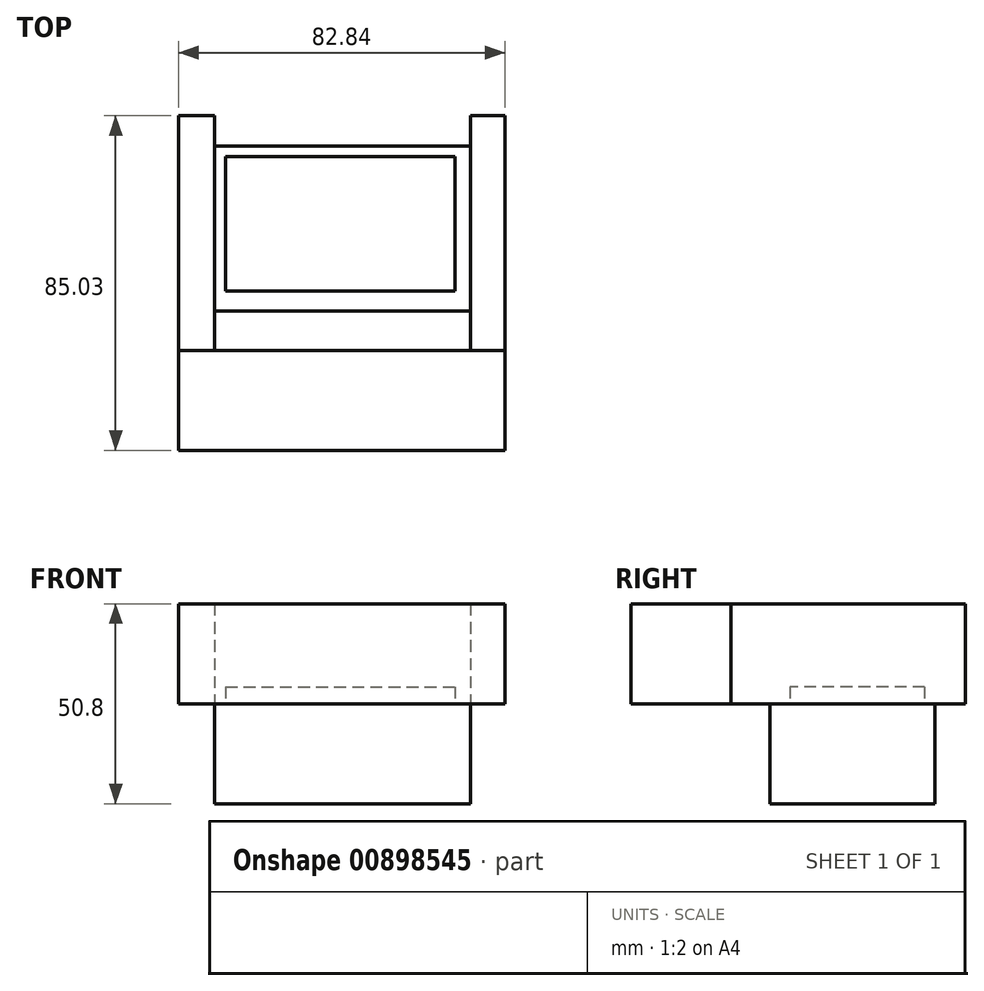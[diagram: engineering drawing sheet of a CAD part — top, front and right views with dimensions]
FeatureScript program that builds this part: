
annotation { "Feature Type Name" : "Feature", "Feature Type Description" : "" }
export const myFeature = defineFeature(function(context is Context, id is Id, definition is map)
    precondition{}
    {
        {
            var Q0;
            Q0=qCreatedBy(makeId("Top.planeOp"),FACE);
            var sketch = newSketch(context, id + "F0", { "sketchPlane" : qUnion([Q0])});
            skLineSegment(sketch, "E0.bottom", {"start": v(-52.18, 30) * mm, "end": v(-43.12, 30) * mm});
            skLineSegment(sketch, "E0.top", {"start": v(-52.18, -29.63) * mm, "end": v(-43.12, -29.63) * mm});
            skLineSegment(sketch, "E0.left", {"start": v(-52.18, 30) * mm, "end": v(-52.18, -29.63) * mm});
            skLineSegment(sketch, "E0.right", {"start": v(-43.12, 30) * mm, "end": v(-43.12, -29.63) * mm});
            skPoint(sketch, "E1.oppositeSnap0", {"position": v(-47.65, -29.63) * mm});
            skLineSegment(sketch, "E1.bottom", {"start": v(21.98, 30) * mm, "end": v(30.66, 30) * mm});
            skLineSegment(sketch, "E1.top", {"start": v(21.98, -29.63) * mm, "end": v(30.66, -29.63) * mm});
            skLineSegment(sketch, "E1.left", {"start": v(21.98, 30) * mm, "end": v(21.98, -29.63) * mm});
            skLineSegment(sketch, "E1.right", {"start": v(30.66, 30) * mm, "end": v(30.66, -29.63) * mm});
            skLineSegment(sketch, "E2.bottom", {"start": v(-43.12, 22.27) * mm, "end": v(21.98, 22.27) * mm});
            skLineSegment(sketch, "E2.top", {"start": v(-43.12, -19.63) * mm, "end": v(21.98, -19.63) * mm});
            skLineSegment(sketch, "E2.left", {"start": v(-43.12, 22.27) * mm, "end": v(-43.12, -19.63) * mm});
            skLineSegment(sketch, "E2.right", {"start": v(21.98, 22.27) * mm, "end": v(21.98, -19.63) * mm});
            skLineSegment(sketch, "E3.bottom", {"start": v(-40.29, 19.63) * mm, "end": v(18.02, 19.63) * mm});
            skLineSegment(sketch, "E3.top", {"start": v(-40.29, -14.53) * mm, "end": v(18.02, -14.53) * mm});
            skLineSegment(sketch, "E3.left", {"start": v(-40.29, 19.63) * mm, "end": v(-40.29, -14.53) * mm});
            skLineSegment(sketch, "E3.right", {"start": v(18.02, 19.63) * mm, "end": v(18.02, -14.53) * mm});
            skSolve(sketch);
        }
        {
            var Q0;
            {var subQ1=sQuery(id+"F0.wireOp",EDGE,"E0.bottom");Q0=makeQuery(id+"F0.imprint","IMPRINT",FACE,{"disambiguationData":[TD([[makeQuery(id+"F0.imprint","IMPRINT",EDGE,{"derivedFrom":subQ1}),-1.0]])]});}
            var Q1;
            {var subQ3=sQuery(id+"F0.wireOp",EDGE,"E1.bottom");Q1=makeQuery(id+"F0.imprint","IMPRINT",FACE,{"disambiguationData":[TD([[makeQuery(id+"F0.imprint","IMPRINT",EDGE,{"derivedFrom":subQ3}),-1.0]])]});}
            extrude(context, id + "F1", {"entities" : qUnion([Q0, Q1]), "depth" : 25.4 * mm});
        }
        {
            var Q0;
            Q0=makeQuery(id+"F0.imprint","IMPRINT",FACE,{"disambiguationData":[TD([[makeQuery(id+"F0.imprint","IMPRINT",EDGE,{"derivedFrom":sQuery(id+"F0.wireOp",EDGE,"E2.bottom")}),-1.0]])]});
            var Q1;
            Q1=makeQuery(id+"F0.imprint","IMPRINT",FACE,{"disambiguationData":[TD([[makeQuery(id+"F0.imprint","IMPRINT",EDGE,{"derivedFrom":sQuery(id+"F0.wireOp",EDGE,"E3.bottom")}),-1.0]])]});
            extrude(context, id + "F2", {"entities" : qUnion([Q0, Q1]), "oppositeDirection" : true, "depth" : 25.4 * mm});
        }
        {
            var Q0;
            Q0=makeQuery(id+"F0.imprint","IMPRINT",FACE,{"disambiguationData":[TD([[makeQuery(id+"F0.imprint","IMPRINT",EDGE,{"derivedFrom":sQuery(id+"F0.wireOp",EDGE,"E3.bottom")}),-1.0]])]});
            extrude(context, id + "F3", {"entities" : qUnion([Q0]), "depth" : 4.32 * mm});
        }
        {
            var Q0;
            Q0=makeQuery(id+"F1.opExtrude","SWEPT_FACE",FACE,{"disambiguationData":[OSD([sQuery(id+"F0.wireOp",EDGE,"E0.top")])]});
            var sketch = newSketch(context, id + "F4", { "sketchPlane" : qUnion([Q0])});
            skLineSegment(sketch, "E4.bottom", {"start": v(-52.18, 0) * mm, "end": v(30.66, 0) * mm});
            skLineSegment(sketch, "E4.top", {"start": v(-52.18, 25.4) * mm, "end": v(30.66, 25.4) * mm});
            skLineSegment(sketch, "E4.left", {"start": v(-52.18, 0) * mm, "end": v(-52.18, 25.4) * mm});
            skLineSegment(sketch, "E4.right", {"start": v(30.66, 0) * mm, "end": v(30.66, 25.4) * mm});
            skSolve(sketch);
        }
        {
            var Q0;
            Q0=qSketchRegion(id+"F4",true);
            extrude(context, id + "F5", {"entities" : qUnion([Q0]), "depth" : 25.4 * mm});
        }
    });
